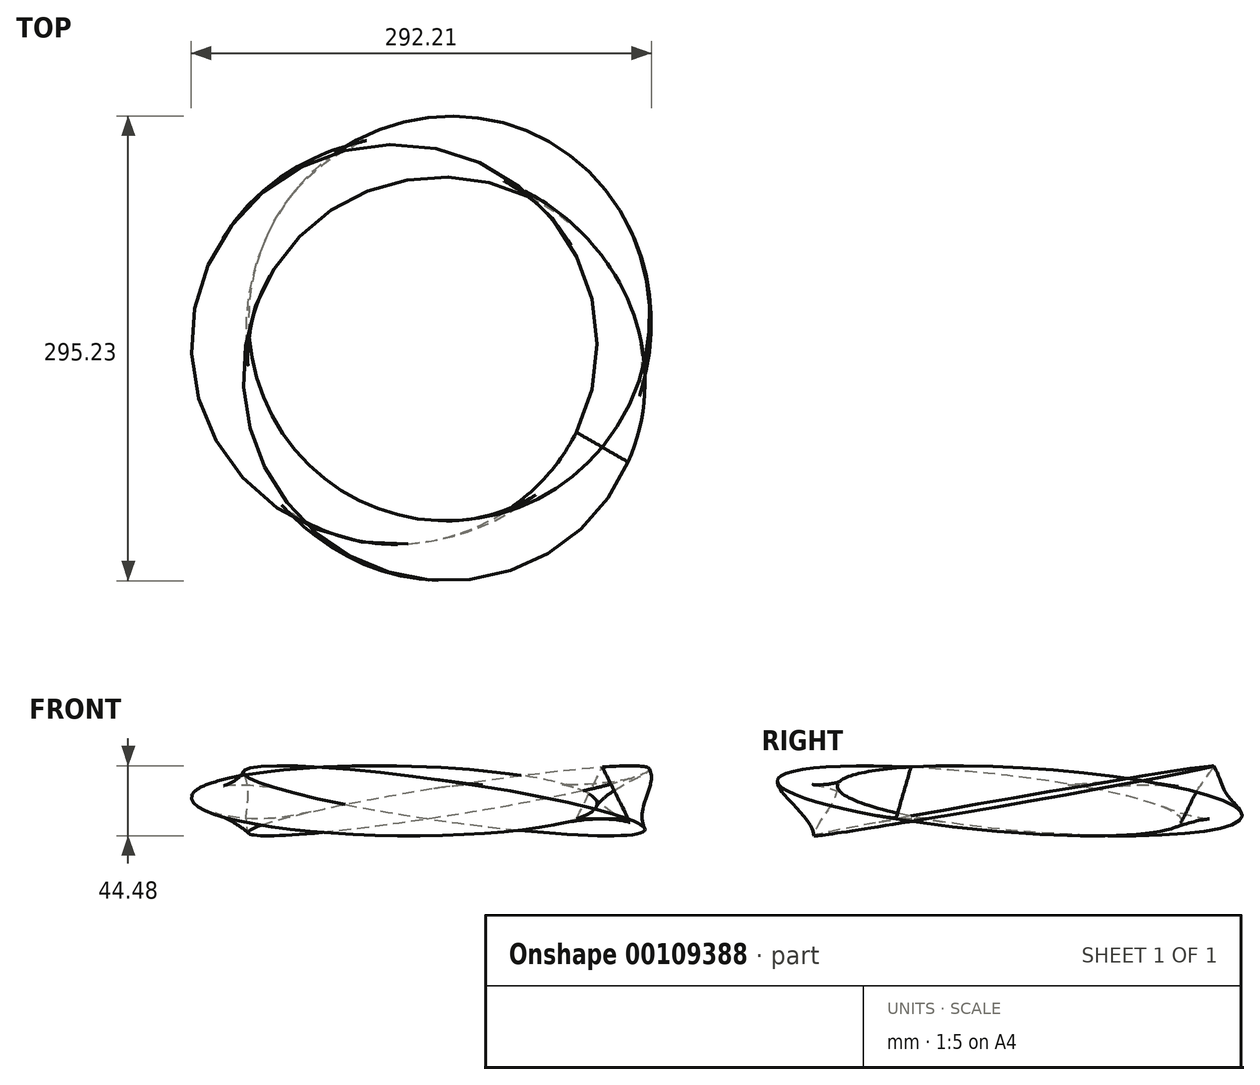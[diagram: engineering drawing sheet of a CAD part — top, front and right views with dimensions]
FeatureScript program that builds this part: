
annotation { "Feature Type Name" : "Feature", "Feature Type Description" : "" }
export const myFeature = defineFeature(function(context is Context, id is Id, definition is map)
    precondition{}
    {
        {
            var Q0;
            Q0=qCreatedBy(makeId("Top.planeOp"),FACE);
            var sketch = newSketch(context, id + "F0", { "sketchPlane" : qUnion([Q0])});
            skCircle(sketch, "E0", {"center": v(0, 0) * mm, "radius": 127 * mm, "construction": true});
            skPoint(sketch, "E1", {"position": v(0, 127) * mm});
            skPoint(sketch, "E2", {"position": v(-109.99, -63.5) * mm});
            skLineSegment(sketch, "E3", {"start": v(0, 127) * mm, "end": v(0, 0) * mm, "construction": true});
            skLineSegment(sketch, "E4", {"start": v(0, 0) * mm, "end": v(-109.99, -63.5) * mm, "construction": true});
            skLineSegment(sketch, "E5.MirrorCS", {"start": v(0, 0) * mm, "end": v(109.99, -63.5) * mm, "construction": true});
            skSolve(sketch);
        }
        {
            var Q0;
            Q0=qCreatedBy(makeId("Front.planeOp"),FACE);
            var Q1;
            Q1=sQuery(id+"F0.wireOp",EDGE,"E4");
            cPlane(context, id + "F1", {"entities" : qUnion([Q0, Q1]), "cplaneType" : CPlaneType.LINE_ANGLE, "offset" : 25.4 * mm, "angle" : 0 * degree, "width" : 152.4 * mm, "height" : 152.4 * mm});
        }
        {
            var Q0;
            Q0=sQuery(id+"F0.wireOp",EDGE,"E5.MirrorCS");
            var Q1;
            Q1=qCreatedBy(makeId("Right.planeOp"),FACE);
            cPlane(context, id + "F2", {"entities" : qUnion([Q0, Q1]), "cplaneType" : CPlaneType.LINE_ANGLE, "offset" : 25.4 * mm, "angle" : 0 * degree, "width" : 152.4 * mm, "height" : 152.4 * mm});
        }
        {
            var Q0;
            Q0=qCreatedBy(id+"F1.planeOp",FACE);
            var sketch = newSketch(context, id + "F3", { "sketchPlane" : qUnion([Q0])});
            skLineSegment(sketch, "E6", {"start": v(127, 22) * mm, "end": v(146.05, -11) * mm});
            skLineSegment(sketch, "E7", {"start": v(146.05, -11) * mm, "end": v(107.95, -11) * mm});
            skLineSegment(sketch, "E8", {"start": v(107.95, -11) * mm, "end": v(127, 22) * mm});
            skLineSegment(sketch, "E9", {"start": v(127, 22) * mm, "end": v(127, 0) * mm, "construction": true});
            skLineSegment(sketch, "E10", {"start": v(127, 0) * mm, "end": v(107.95, -11) * mm, "construction": true});
            skLineSegment(sketch, "E11", {"start": v(127, 0) * mm, "end": v(146.05, -11) * mm, "construction": true});
            skSolve(sketch);
        }
        {
            var Q0;
            Q0=qCreatedBy(makeId("Right.planeOp"),FACE);
            var sketch = newSketch(context, id + "F4", { "sketchPlane" : qUnion([Q0])});
            skLineSegment(sketch, "E12", {"start": v(107.95, -11) * mm, "end": v(127, 22) * mm});
            skLineSegment(sketch, "E13", {"start": v(127, 22) * mm, "end": v(146.05, -11) * mm});
            skLineSegment(sketch, "E14", {"start": v(146.05, -11) * mm, "end": v(107.95, -11) * mm});
            skLineSegment(sketch, "E15", {"start": v(107.95, -11) * mm, "end": v(127, 0) * mm, "construction": true});
            skLineSegment(sketch, "E16", {"start": v(127, 0) * mm, "end": v(146.05, -11) * mm, "construction": true});
            skLineSegment(sketch, "E17", {"start": v(127, 0) * mm, "end": v(127, 22) * mm, "construction": true});
            skSolve(sketch);
        }
        {
            var Q0;
            Q0=qCreatedBy(id+"F2.planeOp",FACE);
            var sketch = newSketch(context, id + "F5", { "sketchPlane" : qUnion([Q0])});
            skLineSegment(sketch, "E18", {"start": v(107.95, -11) * mm, "end": v(127, 22) * mm});
            skLineSegment(sketch, "E19", {"start": v(127, 22) * mm, "end": v(146.05, -11) * mm});
            skLineSegment(sketch, "E20", {"start": v(146.05, -11) * mm, "end": v(107.95, -11) * mm});
            skLineSegment(sketch, "E21", {"start": v(107.95, -11) * mm, "end": v(127, 0) * mm, "construction": true});
            skLineSegment(sketch, "E22", {"start": v(127, 0) * mm, "end": v(146.05, -11) * mm, "construction": true});
            skLineSegment(sketch, "E23", {"start": v(127, 0) * mm, "end": v(127, 22) * mm, "construction": true});
            skSolve(sketch);
        }
        {
            var Q0;
            Q0=sQuery(id+"F3.wireOp",VERTEX,"E9.start");
            var Q1;
            Q1=sQuery(id+"F5.wireOp",VERTEX,"E20.start");
            var Q2;
            Q2=sQuery(id+"F4.wireOp",VERTEX,"E15.start");
            cPlane(context, id + "F6", {"entities" : qUnion([Q0, Q1, Q2]), "cplaneType" : CPlaneType.THREE_POINT, "offset" : 25.4 * mm, "width" : 152.4 * mm, "height" : 152.4 * mm});
        }
        {
            var Q0;
            Q0=qCreatedBy(id+"F6.planeOp",FACE);
            var sketch = newSketch(context, id + "F7", { "sketchPlane" : qUnion([Q0])});
            skCircle(sketch, "E24.converted", {"center": v(9.6, 20.05) * mm, "radius": 128.92 * mm});
            skSolve(sketch);
        }
        {
            var Q0;
            Q0=sQuery(id+"F5.wireOp",VERTEX,"E19.start");
            var Q1;
            Q1=sQuery(id+"F3.wireOp",VERTEX,"E8.start");
            var Q2;
            Q2=sQuery(id+"F4.wireOp",VERTEX,"E16.end");
            cPlane(context, id + "F8", {"entities" : qUnion([Q0, Q1, Q2]), "cplaneType" : CPlaneType.THREE_POINT, "offset" : 25.4 * mm, "width" : 152.4 * mm, "height" : 152.4 * mm});
        }
        {
            var Q0;
            Q0=qCreatedBy(id+"F8.planeOp",FACE);
            var sketch = newSketch(context, id + "F9", { "sketchPlane" : qUnion([Q0])});
            skCircle(sketch, "E25.converted", {"center": v(12.8, 18.18) * mm, "radius": 128.92 * mm});
            skSolve(sketch);
        }
        {
            var Q0;
            Q0=sQuery(id+"F5.wireOp",VERTEX,"E21.start");
            var Q1;
            Q1=sQuery(id+"F3.wireOp",VERTEX,"E6.end");
            var Q2;
            Q2=sQuery(id+"F4.wireOp",VERTEX,"E17.end");
            cPlane(context, id + "F10", {"entities" : qUnion([Q0, Q1, Q2]), "cplaneType" : CPlaneType.THREE_POINT, "offset" : 25.4 * mm, "width" : 152.4 * mm, "height" : 152.4 * mm});
        }
        {
            var Q0;
            Q0=qCreatedBy(id+"F10.planeOp",FACE);
            var sketch = newSketch(context, id + "F11", { "sketchPlane" : qUnion([Q0])});
            skCircle(sketch, "E26.converted", {"center": v(-22.16, 1.9) * mm, "radius": 128.92 * mm});
            skSolve(sketch);
        }
        {
            var Q0;
            Q0=makeQuery(id+"F5.imprint","IMPRINT",FACE,{"disambiguationData":[TD([[makeQuery(id+"F5.imprint","IMPRINT",EDGE,{"derivedFrom":sQuery(id+"F5.wireOp",EDGE,"E18")}),-1.0]])]});
            var Q1;
            Q1=makeQuery(id+"F3.imprint","IMPRINT",FACE,{"disambiguationData":[TD([[makeQuery(id+"F3.imprint","IMPRINT",EDGE,{"derivedFrom":sQuery(id+"F3.wireOp",EDGE,"E6")}),-1.0]])]});
            var Q2;
            Q2=makeQuery(id+"F4.imprint","IMPRINT",FACE,{"disambiguationData":[TD([[makeQuery(id+"F4.imprint","IMPRINT",EDGE,{"derivedFrom":sQuery(id+"F4.wireOp",EDGE,"E12")}),-1.0]])]});
            var Q3;
            Q3=sQuery(id+"F9.wireOp",EDGE,"E25.converted");
            var Q4;
            Q4=sQuery(id+"F7.wireOp",EDGE,"E24.converted");
            var Q5;
            Q5=sQuery(id+"F11.wireOp",EDGE,"E26.converted");
            loft(context, id + "F12", {"addGuides" : true, "sheetProfilesArray" : [{ "sheetProfileEntities" : qUnion([Q0]) }, { "sheetProfileEntities" : qUnion([Q1]) }, { "sheetProfileEntities" : qUnion([Q2]) }], "guidesArray" : [{ "guideEntities" : qUnion([Q3]), "guideDerivativeType" : LoftGuideDerivativeType.DEFAULT, "guideDerivativeMagnitude" : 1 }, { "guideEntities" : qUnion([Q4]), "guideDerivativeType" : LoftGuideDerivativeType.DEFAULT, "guideDerivativeMagnitude" : 1 }, { "guideEntities" : qUnion([Q5]), "guideDerivativeType" : LoftGuideDerivativeType.DEFAULT, "guideDerivativeMagnitude" : 1 }]});
        }
    });
